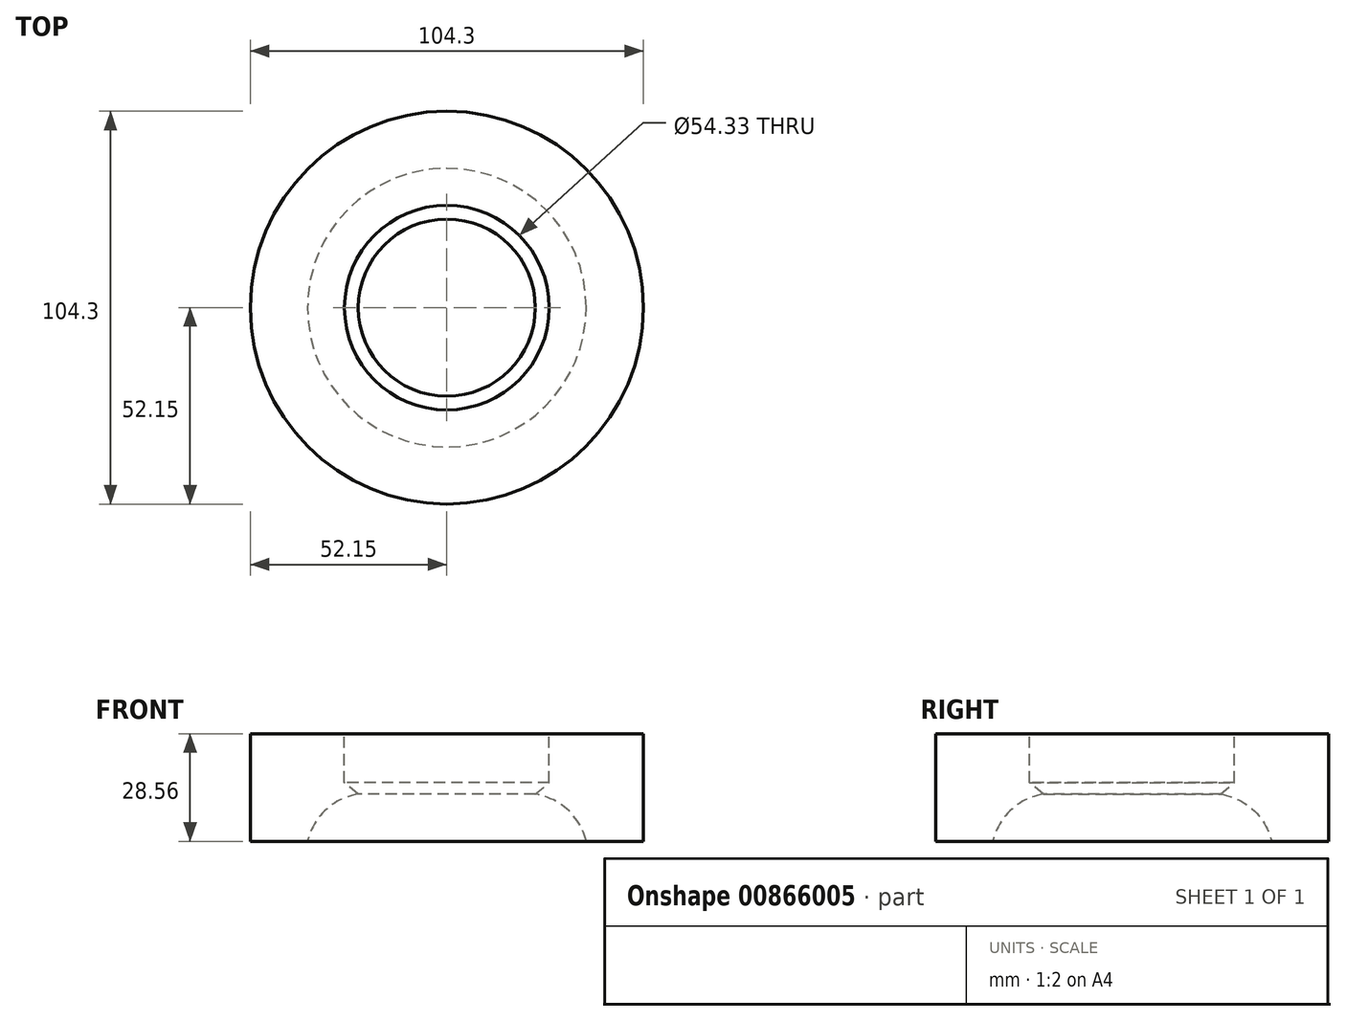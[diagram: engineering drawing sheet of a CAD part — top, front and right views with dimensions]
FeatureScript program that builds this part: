
annotation { "Feature Type Name" : "Feature", "Feature Type Description" : "" }
export const myFeature = defineFeature(function(context is Context, id is Id, definition is map)
    precondition{}
    {
        {
            var Q0;
            Q0=qCreatedBy(makeId("Front.planeOp"),FACE);
            var sketch = newSketch(context, id + "F0", { "sketchPlane" : qUnion([Q0])});
            skLineSegment(sketch, "E0", {"start": v(27.17, 28.56) * mm, "end": v(27.17, 15.6) * mm});
            skLineSegment(sketch, "E1", {"start": v(27.17, 15.6) * mm, "end": v(23.5, 12.5) * mm});
            skArc(sketch, "E2", {"start": v(36.98, 0) * mm, "mid": v(32.17, 8.33) * mm, "end": v(23.5, 12.5) * mm});
            skLineSegment(sketch, "E3", {"start": v(52.15, 28.56) * mm, "end": v(27.17, 28.56) * mm});
            skLineSegment(sketch, "E4", {"start": v(52.15, 0) * mm, "end": v(52.15, 28.56) * mm});
            skLineSegment(sketch, "E5", {"start": v(36.98, 0) * mm, "end": v(52.15, 0) * mm});
            skLineSegment(sketch, "E6", {"start": v(0, 98.93) * mm, "end": v(0, -96.09) * mm});
            skSolve(sketch);
        }
        {
            var Q0;
            Q0=makeQuery(id+"F0.imprint","IMPRINT",FACE,{"disambiguationData":[TD([[makeQuery(id+"F0.imprint","IMPRINT",EDGE,{"derivedFrom":sQuery(id+"F0.wireOp",EDGE,"E0")}),1.0]])]});
            var Q1;
            Q1=sQuery(id+"F0.wireOp",EDGE,"E6");
            revolve(context, id + "F1", {"surfaceOperationType" : NewSurfaceOperationType.NEW, "entities" : qUnion([Q0]), "axis" : qUnion([Q1]), "revolveType" : RevolveType.FULL});
        }
    });
